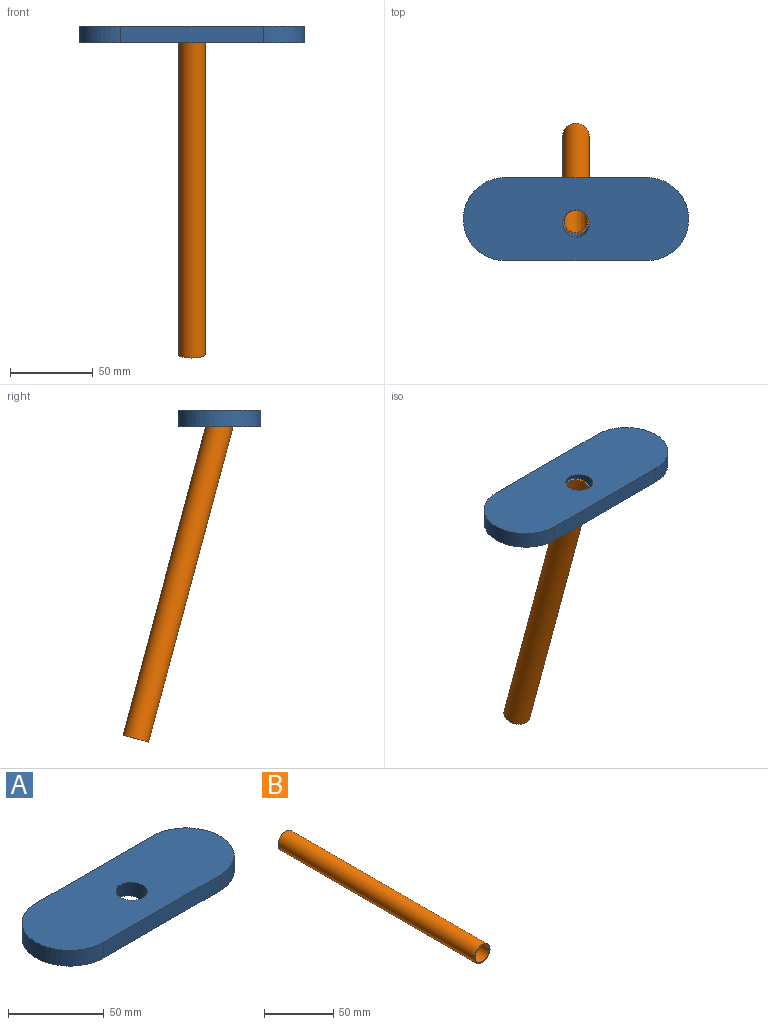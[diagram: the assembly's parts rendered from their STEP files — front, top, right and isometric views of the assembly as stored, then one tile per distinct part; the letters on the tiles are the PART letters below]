
ASSEMBLY  parts=2 mates=1
PART A: 7 faces, bbox 136x50x18.3 mm
  f0: cylinder r=25mm len=50mm, axis (0,0,-1), area 785.4mm2, adj f1,f3,f4,f5
  f1: plane 86x10mm, normal (0,-1,0), area 860mm2, adj f0,f2,f4,f5
  f2: cylinder r=25mm len=50mm, axis (0,0,-1), area 785.4mm2, adj f1,f3,f4,f5
  f3: plane 86x10mm, normal (0,1,0), area 860mm2, adj f0,f2,f4,f5
  f4: plane 136x50mm, normal (0,0,1), area 6055.3mm2, adj f0,f1,f2,f3,f6
  f5: plane 136x50mm, normal (0,0,-1), area 6055.3mm2, adj f0,f1,f2,f3,f6
  f6: cylinder r=8mm len=19.25mm, axis (0,-0.26,0.97), area 520.4mm2, adj f4,f5
PART B: 4 faces, bbox 16x200x16 mm
  f0: cylinder r=7mm len=200mm, axis (0,1,0), area 8796.5mm2, adj f2,f3
  f1: cylinder r=8mm len=200mm, axis (0,1,0), area 10053.1mm2, adj f2,f3
  f2: plane 16x16mm, normal (0,-1,0), area 47.1mm2, adj f0,f1
  f3: plane 16x16mm, normal (0,1,0), area 47.1mm2, adj f0,f1
PLACE A t=(19.86,23.45,12.98)mm
PLACE B rot(axis=(-1,0,0),75deg) t=(19.86,73.88,-175.2)mm
MATE fastened B.f0 <-> A.f6  axis (0,-0.26,0.97) through (19.86,22.11,17.98)mm
